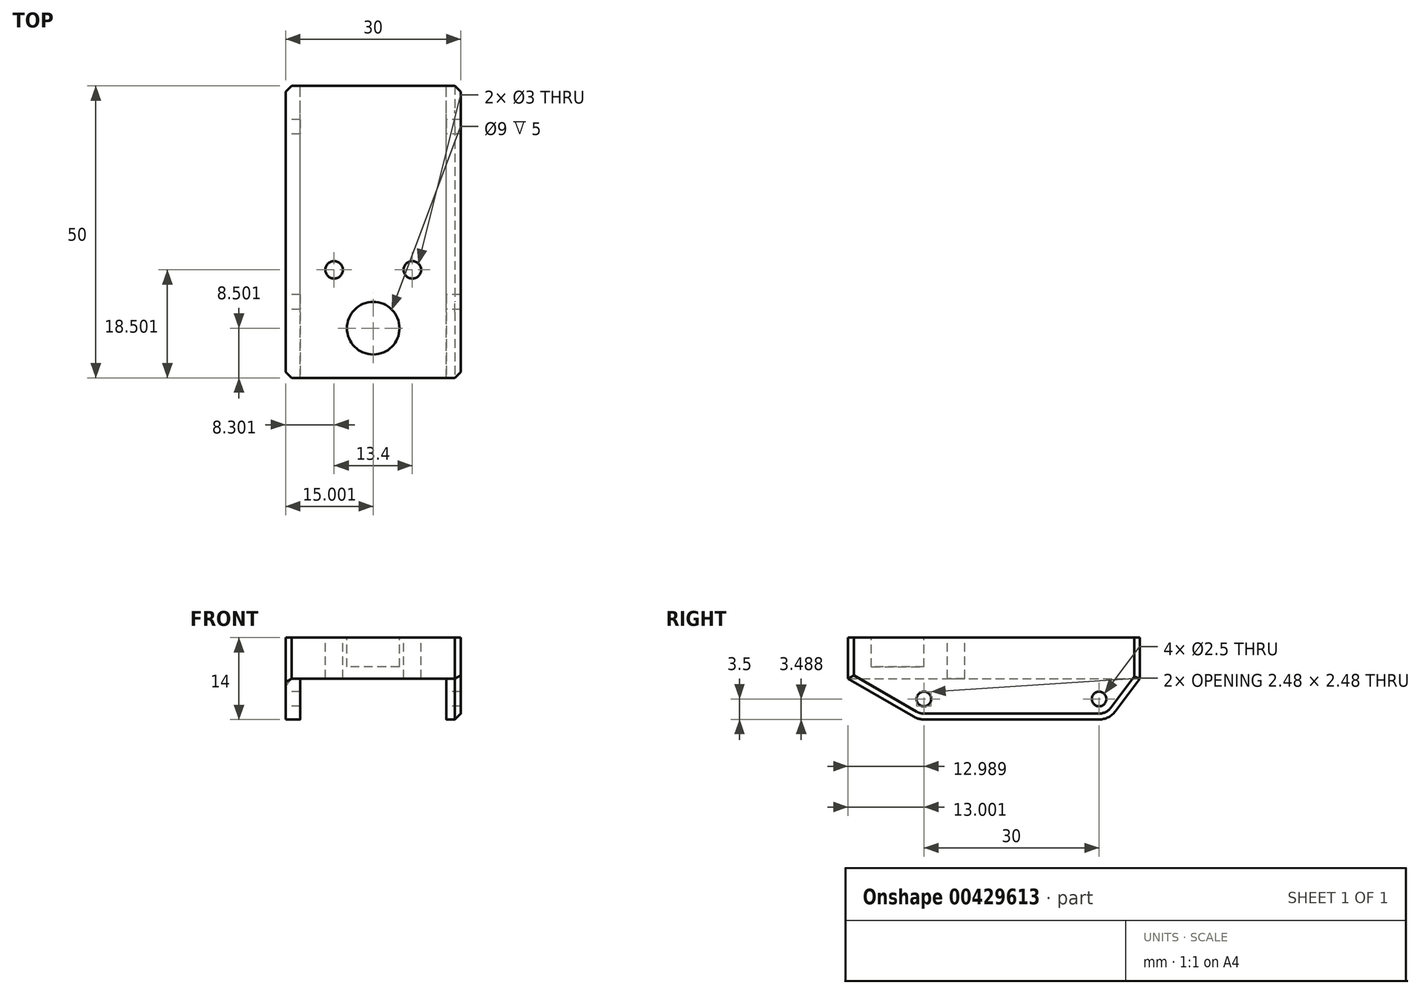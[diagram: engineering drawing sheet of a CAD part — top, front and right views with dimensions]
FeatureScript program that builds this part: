
annotation { "Feature Type Name" : "Feature", "Feature Type Description" : "" }
export const myFeature = defineFeature(function(context is Context, id is Id, definition is map)
    precondition{}
    {
        {
            var Q0;
            Q0=qCreatedBy(makeId("Top.planeOp"),FACE);
            var sketch = newSketch(context, id + "F0", { "sketchPlane" : qUnion([Q0])});
            skLineSegment(sketch, "E0.bottom", {"start": v(-12.34, 22.8) * mm, "end": v(17.66, 22.8) * mm});
            skLineSegment(sketch, "E0.top", {"start": v(-12.34, -27.2) * mm, "end": v(17.66, -27.2) * mm});
            skLineSegment(sketch, "E0.left", {"start": v(-12.34, 22.8) * mm, "end": v(-12.34, -27.2) * mm});
            skLineSegment(sketch, "E0.right", {"start": v(17.66, 22.8) * mm, "end": v(17.66, -27.2) * mm});
            skSolve(sketch);
        }
        {
            var Q0;
            Q0=makeQuery(id+"F0.imprint","IMPRINT",FACE,{"disambiguationData":[TD([[makeQuery(id+"F0.imprint","IMPRINT",EDGE,{"derivedFrom":sQuery(id+"F0.wireOp",EDGE,"E0.bottom")}),-1.0]])]});
            extrude(context, id + "F1", {"entities" : qUnion([Q0]), "depth" : 7 * mm});
        }
        {
            var Q0;
            Q0=makeQuery(id+"F1.opExtrude","CAP_FACE",FACE,{"disambiguationData":[OSD([sQuery(id+"F0.wireOp",EDGE,"E0.bottom"),sQuery(id+"F0.wireOp",EDGE,"E0.top"),sQuery(id+"F0.wireOp",EDGE,"E0.left"),sQuery(id+"F0.wireOp",EDGE,"E0.right")])],"isStart":false});
            var sketch = newSketch(context, id + "F2", { "sketchPlane" : qUnion([Q0])});
            skCircle(sketch, "E1", {"center": v(2.66, -18.7) * mm, "radius": 4.5 * mm});
            skPoint(sketch, "E1.centerSnap0", {"position": v(2.66, -27.2) * mm});
            skSolve(sketch);
        }
        {
            var Q0;
            Q0=makeQuery(id+"F2.imprint","IMPRINT",FACE,{"disambiguationData":[TD([[makeQuery(id+"F2.imprint","IMPRINT",EDGE,{"derivedFrom":sQuery(id+"F2.wireOp",EDGE,"E1")}),1.0]])]});
            extrude(context, id + "F3", {"entities" : qUnion([Q0]), "operationType" : NewBodyOperationType.REMOVE, "oppositeDirection" : true, "depth" : 5 * mm});
        }
        {
            var Q0;
            Q0=makeQuery(id+"F1.opExtrude","CAP_FACE",FACE,{"disambiguationData":[OSD([sQuery(id+"F0.wireOp",EDGE,"E0.bottom"),sQuery(id+"F0.wireOp",EDGE,"E0.top"),sQuery(id+"F0.wireOp",EDGE,"E0.left"),sQuery(id+"F0.wireOp",EDGE,"E0.right")])],"isStart":false});
            var sketch = newSketch(context, id + "F4", { "sketchPlane" : qUnion([Q0])});
            skLineSegment(sketch, "E2", {"start": v(2.66, -27.2) * mm, "end": v(2.66, 22.8) * mm, "construction": true});
            skCircle(sketch, "E3", {"center": v(-4.04, -8.7) * mm, "radius": 1.5 * mm});
            skCircle(sketch, "E4", {"center": v(9.36, -8.7) * mm, "radius": 1.5 * mm});
            skSolve(sketch);
        }
        {
            var Q0;
            Q0=makeQuery(id+"F4.imprint","IMPRINT",FACE,{"disambiguationData":[TD([[makeQuery(id+"F4.imprint","IMPRINT",EDGE,{"derivedFrom":sQuery(id+"F4.wireOp",EDGE,"E4")}),1.0]])]});
            var Q1;
            Q1=makeQuery(id+"F4.imprint","IMPRINT",FACE,{"disambiguationData":[TD([[makeQuery(id+"F4.imprint","IMPRINT",EDGE,{"derivedFrom":sQuery(id+"F4.wireOp",EDGE,"E3")}),1.0]])]});
            extrude(context, id + "F5", {"entities" : qUnion([Q0, Q1]), "operationType" : NewBodyOperationType.REMOVE, "endBound" : BoundingType.THROUGH_ALL, "oppositeDirection" : true, "depth" : 25 * mm});
        }
        {
            var Q0;
            Q0=makeQuery(id+"F1.opExtrude","CAP_FACE",FACE,{"disambiguationData":[OSD([sQuery(id+"F0.wireOp",EDGE,"E0.bottom"),sQuery(id+"F0.wireOp",EDGE,"E0.top"),sQuery(id+"F0.wireOp",EDGE,"E0.left"),sQuery(id+"F0.wireOp",EDGE,"E0.right")])],"isStart":true});
            var sketch = newSketch(context, id + "F6", { "sketchPlane" : qUnion([Q0])});
            skLineSegment(sketch, "E5.bottom", {"start": v(-12.34, 27.2) * mm, "end": v(-9.84, 27.2) * mm});
            skLineSegment(sketch, "E5.top", {"start": v(-12.34, -22.8) * mm, "end": v(-9.84, -22.8) * mm});
            skLineSegment(sketch, "E5.left", {"start": v(-12.34, 27.2) * mm, "end": v(-12.34, -22.8) * mm});
            skLineSegment(sketch, "E5.right", {"start": v(-9.84, 27.2) * mm, "end": v(-9.84, -22.8) * mm});
            skLineSegment(sketch, "E6.bottom", {"start": v(17.66, 27.2) * mm, "end": v(15.16, 27.2) * mm});
            skLineSegment(sketch, "E6.top", {"start": v(17.66, -22.8) * mm, "end": v(15.16, -22.8) * mm});
            skLineSegment(sketch, "E6.left", {"start": v(17.66, 27.2) * mm, "end": v(17.66, -22.8) * mm});
            skLineSegment(sketch, "E6.right", {"start": v(15.16, 27.2) * mm, "end": v(15.16, -22.8) * mm});
            skLineSegment(sketch, "E7.left", {"start": v(-9.84, -19.15) * mm, "end": v(-9.84, -19.87) * mm});
            skLineSegment(sketch, "E7.right", {"start": v(15.16, -19.15) * mm, "end": v(15.16, -19.87) * mm});
            skSolve(sketch);
        }
        {
            var Q0;
            {var subQ1=sQuery(id+"F6.wireOp",EDGE,"E5.bottom");Q0=makeQuery(id+"F6.imprint","IMPRINT",FACE,{"disambiguationData":[TD([[makeQuery(id+"F6.imprint","IMPRINT",EDGE,{"derivedFrom":subQ1}),-1.0]])]});}
            var Q1;
            {var subQ1=sQuery(id+"F6.wireOp",EDGE,"E6.bottom");Q1=makeQuery(id+"F6.imprint","IMPRINT",FACE,{"disambiguationData":[TD([[makeQuery(id+"F6.imprint","IMPRINT",EDGE,{"derivedFrom":subQ1}),-1.0]])]});}
            extrude(context, id + "F7", {"entities" : qUnion([Q0, Q1]), "operationType" : NewBodyOperationType.ADD, "depth" : 7 * mm});
        }
        {
            var Q0;
            Q0=makeQuery(id+"F7.boolean.opBoolean","MERGE",FACE,{"derivedFrom":[makeQuery(id+"F1.opExtrude","SWEPT_FACE",FACE,{"disambiguationData":[OSD([sQuery(id+"F0.wireOp",EDGE,"E0.left")])]}),makeQuery(id+"F7.opExtrude","SWEPT_FACE",FACE,{"disambiguationData":[OSD([sQuery(id+"F6.wireOp",EDGE,"E5.left")])]})]});
            var sketch = newSketch(context, id + "F8", { "sketchPlane" : qUnion([Q0])});
            skCircle(sketch, "E8", {"center": v(14.2, -3.5) * mm, "radius": 1.25 * mm});
            skCircle(sketch, "E9", {"center": v(-15.8, -3.5) * mm, "radius": 1.25 * mm});
            skArc(sketch, "E10", {"start": v(-18.6, -5.6) * mm, "mid": v(-17.36, -6.63) * mm, "end": v(-15.8, -7) * mm});
            skArc(sketch, "E11", {"start": v(14.2, -7) * mm, "mid": v(15.12, -6.88) * mm, "end": v(15.97, -6.53) * mm});
            skLineSegment(sketch, "E12", {"start": v(-22.8, 0) * mm, "end": v(-18.6, -5.6) * mm});
            skLineSegment(sketch, "E13", {"start": v(27.2, 0) * mm, "end": v(15.97, -6.53) * mm});
            skLineSegment(sketch, "E14", {"start": v(-15.8, -7) * mm, "end": v(14.2, -7) * mm});
            skSolve(sketch);
        }
        {
            var Q0;
            {var subQ0=sQuery(id+"F8.wireOp",EDGE,"E10");Q0=makeQuery(id+"F8.imprint","IMPRINT",FACE,{"disambiguationData":[TD([[makeQuery(id+"F8.imprint","IMPRINT",EDGE,{"derivedFrom":subQ0}),-1.0]])]});}
            var Q1;
            {var subQ0=sQuery(id+"F8.wireOp",EDGE,"E11");Q1=makeQuery(id+"F8.imprint","IMPRINT",FACE,{"disambiguationData":[TD([[makeQuery(id+"F8.imprint","IMPRINT",EDGE,{"derivedFrom":subQ0}),-1.0]])]});}
            var Q2;
            Q2=makeQuery(id+"F8.imprint","IMPRINT",FACE,{"disambiguationData":[TD([[makeQuery(id+"F8.imprint","IMPRINT",EDGE,{"derivedFrom":sQuery(id+"F8.wireOp",EDGE,"E8")}),1.0]])]});
            var Q3;
            Q3=makeQuery(id+"F8.imprint","IMPRINT",FACE,{"disambiguationData":[TD([[makeQuery(id+"F8.imprint","IMPRINT",EDGE,{"derivedFrom":sQuery(id+"F8.wireOp",EDGE,"E9")}),1.0]])]});
            extrude(context, id + "F9", {"entities" : qUnion([Q0, Q1, Q2, Q3]), "operationType" : NewBodyOperationType.REMOVE, "endBound" : BoundingType.THROUGH_ALL, "oppositeDirection" : true, "depth" : 25 * mm});
        }
        {
            var Q0;
            Q0=makeQuery(id+"F7.boolean.opBoolean","MERGE",EDGE,{"derivedFrom":[makeQuery(id+"F1.opExtrude","SWEPT_EDGE",EDGE,{"disambiguationData":[OSD([sQuery(id+"F0.wireOp",EDGE,"E0.bottom"),sQuery(id+"F0.wireOp",EDGE,"E0.left")])]}),makeQuery(id+"F7.opExtrude","SWEPT_EDGE",EDGE,{"disambiguationData":[OSD([sQuery(id+"F6.wireOp",EDGE,"E5.top"),sQuery(id+"F6.wireOp",EDGE,"E5.left")])]})]});
            var Q1;
            Q1=makeQuery(id+"F9.boolean.opBoolean","COPY",EDGE,{"derivedFrom":makeQuery(id+"F9.opExtrude","CAP_EDGE",EDGE,{"disambiguationData":[OSD([sQuery(id+"F8.wireOp",EDGE,"E12")])],"isStart":true})});
            var Q2;
            Q2=makeQuery(id+"F7.boolean.opBoolean","MERGE",EDGE,{"derivedFrom":[makeQuery(id+"F1.opExtrude","SWEPT_EDGE",EDGE,{"disambiguationData":[OSD([sQuery(id+"F0.wireOp",EDGE,"E0.top"),sQuery(id+"F0.wireOp",EDGE,"E0.left")])]}),makeQuery(id+"F7.opExtrude","SWEPT_EDGE",EDGE,{"disambiguationData":[OSD([sQuery(id+"F6.wireOp",EDGE,"E5.bottom"),sQuery(id+"F6.wireOp",EDGE,"E5.left")])]})]});
            var Q3;
            Q3=makeQuery(id+"F7.boolean.opBoolean","MERGE",EDGE,{"derivedFrom":[makeQuery(id+"F1.opExtrude","SWEPT_EDGE",EDGE,{"disambiguationData":[OSD([sQuery(id+"F0.wireOp",EDGE,"E0.top"),sQuery(id+"F0.wireOp",EDGE,"E0.right")])]}),makeQuery(id+"F7.opExtrude","SWEPT_EDGE",EDGE,{"disambiguationData":[OSD([sQuery(id+"F6.wireOp",EDGE,"E6.bottom"),sQuery(id+"F6.wireOp",EDGE,"E6.left")])]})]});
            var Q4;
            Q4=makeQuery(id+"F9.boolean.opBoolean","INTERSECT",EDGE,{"derivedFrom":[makeQuery(id+"F7.boolean.opBoolean","MERGE",FACE,{"derivedFrom":[makeQuery(id+"F1.opExtrude","SWEPT_FACE",FACE,{"disambiguationData":[OSD([sQuery(id+"F0.wireOp",EDGE,"E0.right")])]}),makeQuery(id+"F7.opExtrude","SWEPT_FACE",FACE,{"disambiguationData":[OSD([sQuery(id+"F6.wireOp",EDGE,"E6.left")])]})]}),makeQuery(id+"F9.opExtrude","SWEPT_FACE",FACE,{"disambiguationData":[OSD([sQuery(id+"F8.wireOp",EDGE,"E13")])]})]});
            var Q5;
            Q5=makeQuery(id+"F7.boolean.opBoolean","MERGE",EDGE,{"derivedFrom":[makeQuery(id+"F1.opExtrude","SWEPT_EDGE",EDGE,{"disambiguationData":[OSD([sQuery(id+"F0.wireOp",EDGE,"E0.bottom"),sQuery(id+"F0.wireOp",EDGE,"E0.right")])]}),makeQuery(id+"F7.opExtrude","SWEPT_EDGE",EDGE,{"disambiguationData":[OSD([sQuery(id+"F6.wireOp",EDGE,"E6.top"),sQuery(id+"F6.wireOp",EDGE,"E6.left")])]})]});
            var Q6;
            Q6=makeQuery(id+"F3.boolean.opBoolean","COPY",EDGE,{"derivedFrom":makeQuery(id+"F3.opExtrude","CAP_EDGE",EDGE,{"disambiguationData":[OSD([sQuery(id+"F2.wireOp",EDGE,"E1")])],"isStart":true})});
            var Q7;
            Q7=makeQuery(id+"F5.boolean.opBoolean","COPY",EDGE,{"derivedFrom":makeQuery(id+"F5.opExtrude","CAP_EDGE",EDGE,{"disambiguationData":[OSD([sQuery(id+"F4.wireOp",EDGE,"E3")])],"isStart":true})});
            var Q8;
            Q8=makeQuery(id+"F5.boolean.opBoolean","COPY",EDGE,{"derivedFrom":makeQuery(id+"F5.opExtrude","CAP_EDGE",EDGE,{"disambiguationData":[OSD([sQuery(id+"F4.wireOp",EDGE,"E4")])],"isStart":true})});
            chamfer(context, id + "F10", {"entities" : qUnion([Q0, Q1, Q2, Q3, Q4, Q5, Q6, Q7, Q8]), "width" : 1 * mm, "tangentPropagation" : true});
        }
    });
